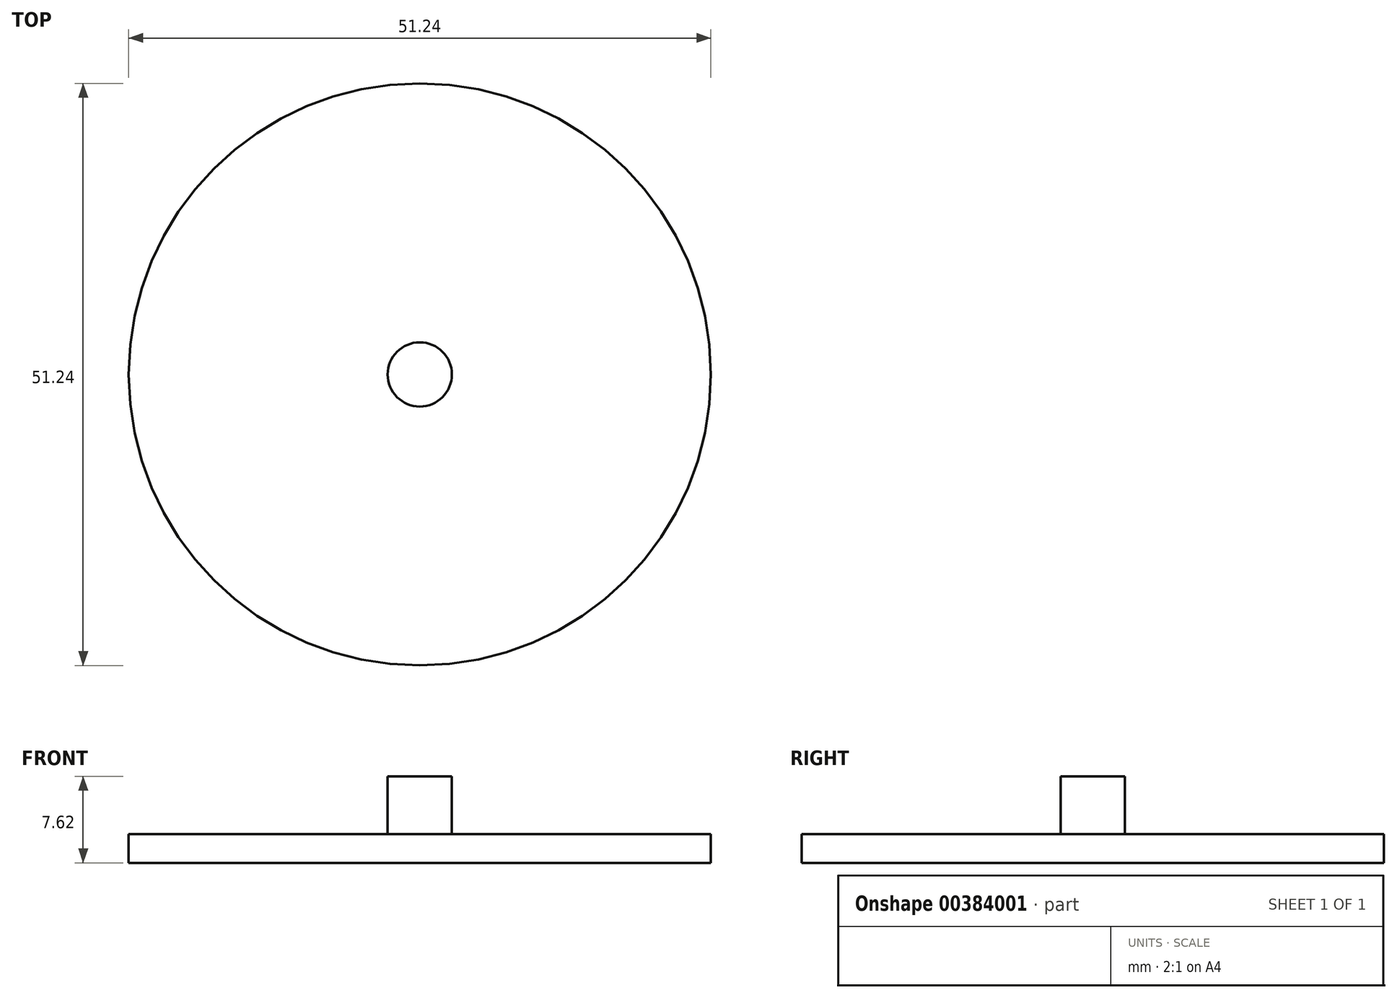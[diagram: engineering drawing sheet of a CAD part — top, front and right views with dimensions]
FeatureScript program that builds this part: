
annotation { "Feature Type Name" : "Feature", "Feature Type Description" : "" }
export const myFeature = defineFeature(function(context is Context, id is Id, definition is map)
    precondition{}
    {
        {
            var Q0;
            Q0=qCreatedBy(makeId("Top.planeOp"),FACE);
            var sketch = newSketch(context, id + "F0", { "sketchPlane" : qUnion([Q0])});
            skCircle(sketch, "E0", {"center": v(0, 0) * mm, "radius": 25.62 * mm});
            skSolve(sketch);
        }
        {
            var Q0;
            Q0=makeQuery(id+"F0.imprint","IMPRINT",FACE,{"disambiguationData":[TD([[makeQuery(id+"F0.imprint","IMPRINT",EDGE,{"derivedFrom":sQuery(id+"F0.wireOp",EDGE,"E0")}),1.0]])]});
            extrude(context, id + "F1", {"entities" : qUnion([Q0]), "depth" : 2.54 * mm, "offsetDistance" : 25.4 * mm});
        }
        {
            var Q0;
            Q0=qCreatedBy(makeId("Top.planeOp"),FACE);
            var sketch = newSketch(context, id + "F2", { "sketchPlane" : qUnion([Q0])});
            skCircle(sketch, "E1", {"center": v(0, 0) * mm, "radius": 2.83 * mm});
            skSolve(sketch);
        }
        {
            var Q0;
            Q0 = qSketchRegion(id + "F2", true);
            extrude(context, id + "F3", {"entities" : qUnion([Q0]), "operationType" : NewBodyOperationType.ADD, "depth" : 7.62 * mm, "offsetDistance" : 25.4 * mm});
        }
    });
